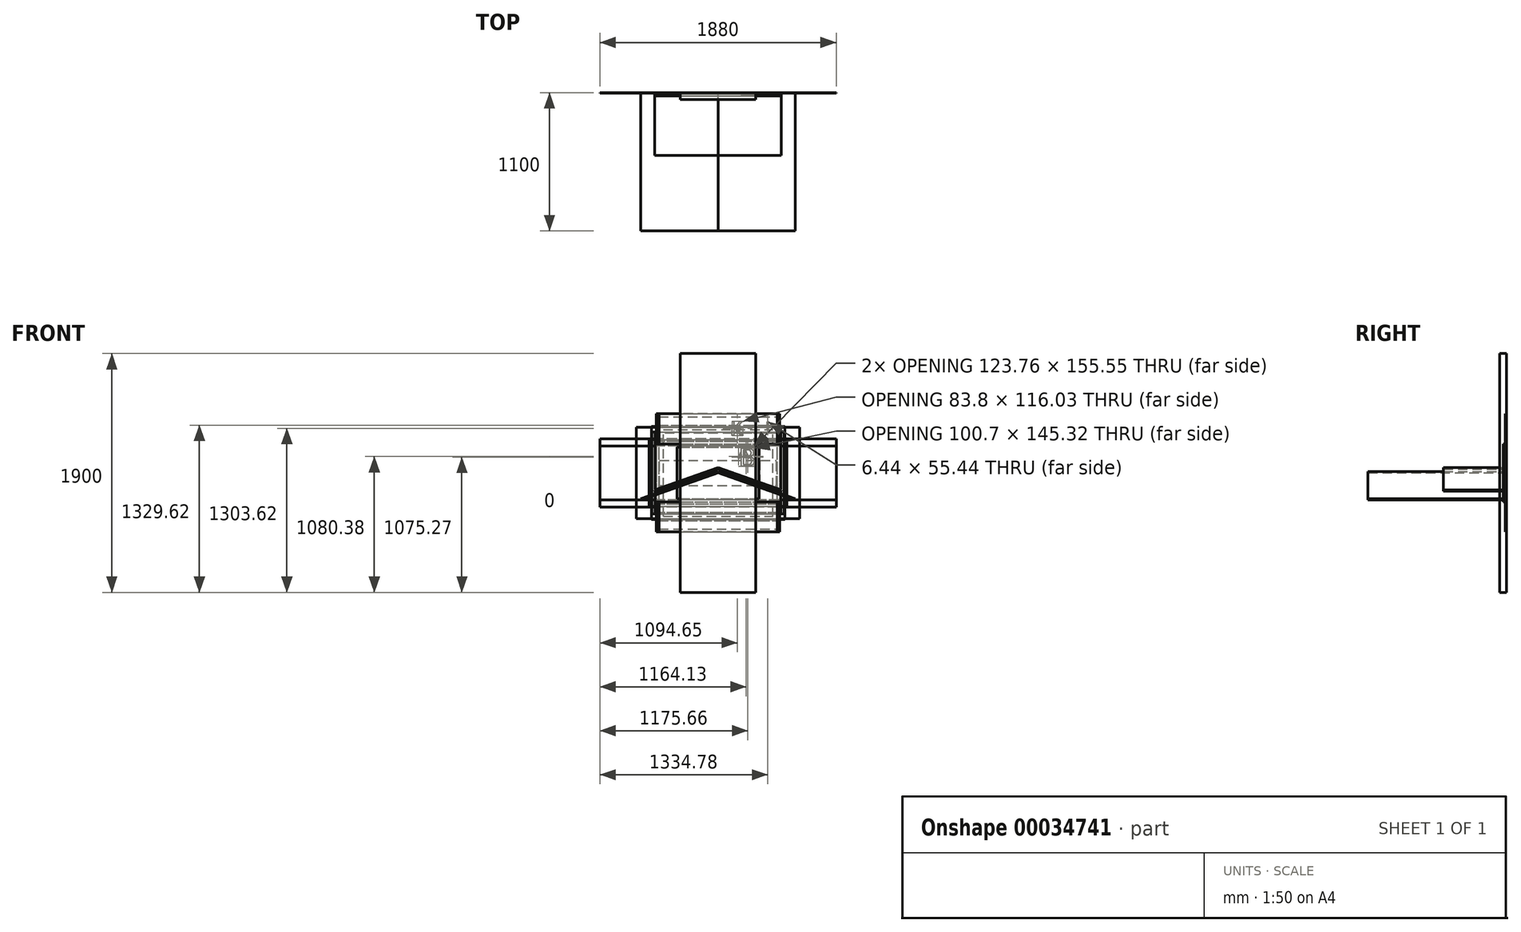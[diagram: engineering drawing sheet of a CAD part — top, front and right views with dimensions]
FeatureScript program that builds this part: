
annotation { "Feature Type Name" : "Feature", "Feature Type Description" : "" }
export const myFeature = defineFeature(function(context is Context, id is Id, definition is map)
    precondition{}
    {
        {
            var Q0;
            Q0=qCreatedBy(makeId("Front.planeOp"),FACE);
            var sketch = newSketch(context, id + "F0", { "sketchPlane" : qUnion([Q0])});
            skLineSegment(sketch, "E0.rect.bottom", {"start": v(500, 315) * mm, "end": v(-500, 315) * mm});
            skLineSegment(sketch, "E0.rect.top", {"start": v(500, -315) * mm, "end": v(-500, -315) * mm});
            skLineSegment(sketch, "E0.rect.left", {"start": v(500, 315) * mm, "end": v(500, -315) * mm});
            skLineSegment(sketch, "E0.rect.right", {"start": v(-500, 315) * mm, "end": v(-500, -315) * mm});
            skPoint(sketch, "E0.rect.middle", {"position": v(0, 0) * mm});
            skSolve(sketch);
        }
        {
            var Q0;
            Q0 = qSketchRegion(id + "F0", true);
            extrude(context, id + "F1", {"entities" : qUnion([Q0]), "depth" : 5 * mm});
        }
        {
            var Q0;
            Q0=makeQuery(id+"F1.opExtrude","CAP_FACE",FACE,{"disambiguationData":[OSD([sQuery(id+"F0.wireOp",EDGE,"E0.rect.bottom"),sQuery(id+"F0.wireOp",EDGE,"E0.rect.top"),sQuery(id+"F0.wireOp",EDGE,"E0.rect.left"),sQuery(id+"F0.wireOp",EDGE,"E0.rect.right")])],"isStart":false});
            var sketch = newSketch(context, id + "F2", { "sketchPlane" : qUnion([Q0])});
            skLineSegment(sketch, "E1.rect.bottom", {"start": v(-470, -470) * mm, "end": v(470, -470) * mm});
            skLineSegment(sketch, "E1.rect.top", {"start": v(-470, 470) * mm, "end": v(470, 470) * mm});
            skLineSegment(sketch, "E1.rect.left", {"start": v(-470, -470) * mm, "end": v(-470, 470) * mm});
            skLineSegment(sketch, "E1.rect.right", {"start": v(470, -470) * mm, "end": v(470, 470) * mm});
            skPoint(sketch, "E1.rect.middle", {"position": v(0, 0) * mm});
            skSolve(sketch);
        }
        {
            var Q0;
            Q0 = qSketchRegion(id + "F2", true);
            extrude(context, id + "F3", {"entities" : qUnion([Q0]), "depth" : 5 * mm});
        }
        {
            var Q0;
            Q0=qCreatedBy(makeId("Front.planeOp"),FACE);
            var sketch = newSketch(context, id + "F4", { "sketchPlane" : qUnion([Q0])});
            skLineSegment(sketch, "E2.rect.bottom", {"start": v(-500, -230) * mm, "end": v(500, -230) * mm});
            skLineSegment(sketch, "E2.rect.top", {"start": v(-500, 230) * mm, "end": v(500, 230) * mm});
            skLineSegment(sketch, "E2.rect.left", {"start": v(-500, -230) * mm, "end": v(-500, 230) * mm});
            skLineSegment(sketch, "E2.rect.right", {"start": v(500, -230) * mm, "end": v(500, 230) * mm});
            skPoint(sketch, "E2.rect.middle", {"position": v(0, 0) * mm});
            skSolve(sketch);
        }
        {
            var Q0;
            Q0 = qSketchRegion(id + "F4", true);
            extrude(context, id + "F5", {"entities" : qUnion([Q0]), "depth" : 25 * mm});
        }
        {
            var Q0;
            Q0=qCreatedBy(makeId("Front.planeOp"),FACE);
            var sketch = newSketch(context, id + "F6", { "sketchPlane" : qUnion([Q0])});
            skLineSegment(sketch, "E3.rect.bottom", {"start": v(500, -250) * mm, "end": v(-500, -250) * mm});
            skLineSegment(sketch, "E3.rect.top", {"start": v(500, 250) * mm, "end": v(-500, 250) * mm});
            skLineSegment(sketch, "E3.rect.left", {"start": v(500, -250) * mm, "end": v(500, 250) * mm});
            skLineSegment(sketch, "E3.rect.right", {"start": v(-500, -250) * mm, "end": v(-500, 250) * mm});
            skPoint(sketch, "E3.rect.middle", {"position": v(0, 0) * mm});
            skSolve(sketch);
        }
        {
            var Q0;
            Q0 = qSketchRegion(id + "F6", true);
            extrude(context, id + "F7", {"entities" : qUnion([Q0]), "depth" : 5 * mm});
        }
        {
            var Q0;
            {var subQ0=makeQuery(id+"F1.opExtrude","CAP_EDGE",EDGE,{"disambiguationData":[OSD([sQuery(id+"F0.wireOp",EDGE,"E0.rect.top")])],"isStart":false});var subQ3=sQuery(id+"F2.wireOp",EDGE,"E1.rect.left");var subQ4=makeQuery(id+"F2.imprint","INTERSECT",VERTEX,{"derivedFrom":[subQ0,subQ3]});Q0=makeQuery(id+"F2.imprint","IMPRINT",FACE,{"disambiguationData":[TD([[makeQuery(id+"F2.imprint","IMPRINT",EDGE,{"disambiguationData":[TD([[subQ4,-1.0]])],"derivedFrom":subQ3}),-1.0]])]});}
            var sketch = newSketch(context, id + "F8", { "sketchPlane" : qUnion([Q0])});
            skText(sketch, "E4", { "text": "A", "fontName": "OpenSans-Regular.ttf"});
            const initialGuessF8  = {"E4": [0.16225, 0.1153, 1, 0, 0.09326]};
            skSetInitialGuess(sketch, initialGuessF8);
            skSolve(sketch);
        }
        {
            var Q0;
            Q0=makeQuery(id+"F8.imprint","IMPRINT",FACE,{"disambiguationData":[TD([[makeQuery(id+"F8.imprint","IMPRINT",EDGE,{"derivedFrom":sQuery(id+"F8.wireOp",EDGE,"E4.sketch_text.stroke-0")}),-1.0]])]});
            extrude(context, id + "F9", {"entities" : qUnion([Q0]), "operationType" : NewBodyOperationType.REMOVE, "oppositeDirection" : true, "depth" : 25 * mm});
        }
        {
            var Q0;
            Q0=makeQuery(id+"F3.opExtrude","CAP_FACE",FACE,{"disambiguationData":[OSD([sQuery(id+"F2.wireOp",EDGE,"E1.rect.bottom"),sQuery(id+"F2.wireOp",EDGE,"E1.rect.top"),sQuery(id+"F2.wireOp",EDGE,"E1.rect.left"),sQuery(id+"F2.wireOp",EDGE,"E1.rect.right")])],"isStart":false});
            var sketch = newSketch(context, id + "F10", { "sketchPlane" : qUnion([Q0])});
            skText(sketch, "E5", { "text": "K", "fontName": "OpenSans-Regular.ttf"});
            const initialGuessF10  = {"E5": [0.0968, 0.2956, 1, 0, 0.11702]};
            skSetInitialGuess(sketch, initialGuessF10);
            skSolve(sketch);
        }
        {
            var Q0;
            Q0 = qSketchRegion(id + "F10", true);
            extrude(context, id + "F11", {"entities" : qUnion([Q0]), "operationType" : NewBodyOperationType.REMOVE, "oppositeDirection" : true, "depth" : 25 * mm});
        }
        {
            var Q0;
            Q0=makeQuery(id+"F5.opExtrude","CAP_FACE",FACE,{"disambiguationData":[OSD([sQuery(id+"F4.wireOp",EDGE,"E2.rect.bottom"),sQuery(id+"F4.wireOp",EDGE,"E2.rect.top"),sQuery(id+"F4.wireOp",EDGE,"E2.rect.left"),sQuery(id+"F4.wireOp",EDGE,"E2.rect.right")])],"isStart":false});
            var sketch = newSketch(context, id + "F12", { "sketchPlane" : qUnion([Q0])});
            skText(sketch, "E6", { "text": "B", "fontName": "OpenSans-Regular.ttf"});
            const initialGuessF12  = {"E6": [0.16534, 0.05261, 1, 0, 0.14656]};
            skSetInitialGuess(sketch, initialGuessF12);
            skSolve(sketch);
        }
        {
            var Q0;
            Q0 = qSketchRegion(id + "F12", true);
            extrude(context, id + "F13", {"entities" : qUnion([Q0]), "operationType" : NewBodyOperationType.REMOVE, "oppositeDirection" : true, "depth" : 25 * mm});
        }
        {
            var Q0;
            Q0=qCreatedBy(makeId("Front.planeOp"),FACE);
            var sketch = newSketch(context, id + "F14", { "sketchPlane" : qUnion([Q0])});
            skLineSegment(sketch, "E7.rect.bottom", {"start": v(-435, -345) * mm, "end": v(435, -345) * mm});
            skLineSegment(sketch, "E7.rect.top", {"start": v(-435, 345) * mm, "end": v(435, 345) * mm});
            skLineSegment(sketch, "E7.rect.left", {"start": v(-435, -345) * mm, "end": v(-435, 345) * mm});
            skLineSegment(sketch, "E7.rect.right", {"start": v(435, -345) * mm, "end": v(435, 345) * mm});
            skPoint(sketch, "E7.rect.middle", {"position": v(0, 0) * mm});
            skSolve(sketch);
        }
        {
            var Q0;
            Q0 = qSketchRegion(id + "F14", true);
            extrude(context, id + "F15", {"entities" : qUnion([Q0]), "depth" : 5 * mm});
        }
        {
            var Q0;
            Q0=qCreatedBy(makeId("Front.planeOp"),FACE);
            var sketch = newSketch(context, id + "F16", { "sketchPlane" : qUnion([Q0])});
            skLineSegment(sketch, "E8.rect.bottom", {"start": v(-490, 380) * mm, "end": v(490, 380) * mm});
            skLineSegment(sketch, "E8.rect.top", {"start": v(-490, -380) * mm, "end": v(490, -380) * mm});
            skLineSegment(sketch, "E8.rect.left", {"start": v(-490, 380) * mm, "end": v(-490, -380) * mm});
            skLineSegment(sketch, "E8.rect.right", {"start": v(490, 380) * mm, "end": v(490, -380) * mm});
            skPoint(sketch, "E8.rect.middle", {"position": v(0, 0) * mm});
            skSolve(sketch);
        }
        {
            var Q0;
            Q0 = qSketchRegion(id + "F16", true);
            extrude(context, id + "F17", {"entities" : qUnion([Q0]), "depth" : 5 * mm});
        }
        {
            var Q0;
            Q0=qCreatedBy(makeId("Front.planeOp"),FACE);
            var sketch = newSketch(context, id + "F18", { "sketchPlane" : qUnion([Q0])});
            skLineSegment(sketch, "E9.rect.bottom", {"start": v(-530, 370) * mm, "end": v(530, 370) * mm});
            skLineSegment(sketch, "E9.rect.top", {"start": v(-530, -370) * mm, "end": v(530, -370) * mm});
            skLineSegment(sketch, "E9.rect.left", {"start": v(-530, 370) * mm, "end": v(-530, -370) * mm});
            skLineSegment(sketch, "E9.rect.right", {"start": v(530, 370) * mm, "end": v(530, -370) * mm});
            skPoint(sketch, "E9.rect.middle", {"position": v(0, 0) * mm});
            skSolve(sketch);
        }
        {
            var Q0;
            Q0 = qSketchRegion(id + "F18", true);
            extrude(context, id + "F19", {"entities" : qUnion([Q0]), "depth" : 5 * mm});
        }
        {
            var Q0;
            Q0=qCreatedBy(makeId("Front.planeOp"),FACE);
            var sketch = newSketch(context, id + "F20", { "sketchPlane" : qUnion([Q0])});
            skLineSegment(sketch, "E10.rect.bottom", {"start": v(-325, 205) * mm, "end": v(325, 205) * mm});
            skLineSegment(sketch, "E10.rect.top", {"start": v(-325, -205) * mm, "end": v(325, -205) * mm});
            skLineSegment(sketch, "E10.rect.left", {"start": v(-325, 205) * mm, "end": v(-325, -205) * mm});
            skLineSegment(sketch, "E10.rect.right", {"start": v(325, 205) * mm, "end": v(325, -205) * mm});
            skPoint(sketch, "E10.rect.middle", {"position": v(0, 0) * mm});
            skSolve(sketch);
        }
        {
            var Q0;
            Q0 = qSketchRegion(id + "F20", true);
            extrude(context, id + "F21", {"entities" : qUnion([Q0]), "depth" : 25 * mm});
        }
        {
            var Q0;
            Q0=qCreatedBy(makeId("Front.planeOp"),FACE);
            var sketch = newSketch(context, id + "F22", { "sketchPlane" : qUnion([Q0])});
            skLineSegment(sketch, "E11.rect.bottom", {"start": v(-525, -325) * mm, "end": v(525, -325) * mm});
            skLineSegment(sketch, "E11.rect.top", {"start": v(-525, 325) * mm, "end": v(525, 325) * mm});
            skLineSegment(sketch, "E11.rect.left", {"start": v(-525, -325) * mm, "end": v(-525, 325) * mm});
            skLineSegment(sketch, "E11.rect.right", {"start": v(525, -325) * mm, "end": v(525, 325) * mm});
            skPoint(sketch, "E11.rect.middle", {"position": v(0, 0) * mm});
            skSolve(sketch);
        }
        {
            var Q0;
            Q0 = qSketchRegion(id + "F22", true);
            extrude(context, id + "F23", {"entities" : qUnion([Q0]), "depth" : 5 * mm});
        }
        {
            var Q0;
            Q0=qCreatedBy(makeId("Front.planeOp"),FACE);
            var sketch = newSketch(context, id + "F24", { "sketchPlane" : qUnion([Q0])});
            skLineSegment(sketch, "E12.rect.bottom", {"start": v(490, 470) * mm, "end": v(-490, 470) * mm});
            skLineSegment(sketch, "E12.rect.top", {"start": v(490, -470) * mm, "end": v(-490, -470) * mm});
            skLineSegment(sketch, "E12.rect.left", {"start": v(490, 470) * mm, "end": v(490, -470) * mm});
            skLineSegment(sketch, "E12.rect.right", {"start": v(-490, 470) * mm, "end": v(-490, -470) * mm});
            skPoint(sketch, "E12.rect.middle", {"position": v(0, 0) * mm});
            skSolve(sketch);
        }
        {
            var Q0;
            Q0 = qSketchRegion(id + "F24", true);
            extrude(context, id + "F25", {"entities" : qUnion([Q0]), "depth" : 5 * mm});
        }
        {
            var Q0;
            Q0=makeQuery(id+"F25.opExtrude","CAP_FACE",FACE,{"disambiguationData":[OSD([sQuery(id+"F24.wireOp",EDGE,"E12.rect.bottom"),sQuery(id+"F24.wireOp",EDGE,"E12.rect.top"),sQuery(id+"F24.wireOp",EDGE,"E12.rect.left"),sQuery(id+"F24.wireOp",EDGE,"E12.rect.right")])],"isStart":false});
            var sketch = newSketch(context, id + "F26", { "sketchPlane" : qUnion([Q0])});
            skText(sketch, "E13", { "text": "I", "fontName": "OpenSans-Regular.ttf"});
            const initialGuessF26  = {"E13": [0.38394, 0.3519, 1, 0, 0.05591]};
            skSetInitialGuess(sketch, initialGuessF26);
            skSolve(sketch);
        }
        {
            var Q0;
            Q0 = qSketchRegion(id + "F26", true);
            extrude(context, id + "F27", {"entities" : qUnion([Q0]), "operationType" : NewBodyOperationType.REMOVE, "oppositeDirection" : true, "depth" : 25 * mm});
        }
        {
            var Q0;
            Q0=qCreatedBy(makeId("Front.planeOp"),FACE);
            var sketch = newSketch(context, id + "F28", { "sketchPlane" : qUnion([Q0])});
            skLineSegment(sketch, "E14.rect.bottom", {"start": v(-470, -445) * mm, "end": v(470, -445) * mm});
            skLineSegment(sketch, "E14.rect.top", {"start": v(-470, 445) * mm, "end": v(470, 445) * mm});
            skLineSegment(sketch, "E14.rect.left", {"start": v(-470, -445) * mm, "end": v(-470, 445) * mm});
            skLineSegment(sketch, "E14.rect.right", {"start": v(470, -445) * mm, "end": v(470, 445) * mm});
            skPoint(sketch, "E14.rect.middle", {"position": v(0, 0) * mm});
            skSolve(sketch);
        }
        {
            var Q0;
            Q0 = qSketchRegion(id + "F28", true);
            extrude(context, id + "F29", {"entities" : qUnion([Q0]), "depth" : 5 * mm});
        }
        {
            var Q0;
            Q0=qCreatedBy(makeId("Front.planeOp"),FACE);
            var sketch = newSketch(context, id + "F30", { "sketchPlane" : qUnion([Q0])});
            skLineSegment(sketch, "E15.rect.bottom", {"start": v(-650, -365) * mm, "end": v(650, -365) * mm});
            skLineSegment(sketch, "E15.rect.top", {"start": v(-650, 365) * mm, "end": v(650, 365) * mm});
            skLineSegment(sketch, "E15.rect.left", {"start": v(-650, -365) * mm, "end": v(-650, 365) * mm});
            skLineSegment(sketch, "E15.rect.right", {"start": v(650, -365) * mm, "end": v(650, 365) * mm});
            skPoint(sketch, "E15.rect.middle", {"position": v(0, 0) * mm});
            skSolve(sketch);
        }
        {
            var Q0;
            Q0 = qSketchRegion(id + "F30", true);
            extrude(context, id + "F31", {"entities" : qUnion([Q0]), "depth" : 5 * mm});
        }
        {
            var Q0;
            Q0=qCreatedBy(makeId("Front.planeOp"),FACE);
            var sketch = newSketch(context, id + "F32", { "sketchPlane" : qUnion([Q0])});
            skLineSegment(sketch, "E16.rect.bottom", {"start": v(-547.5, 265) * mm, "end": v(547.5, 265) * mm});
            skLineSegment(sketch, "E16.rect.top", {"start": v(-547.5, -265) * mm, "end": v(547.5, -265) * mm});
            skLineSegment(sketch, "E16.rect.left", {"start": v(-547.5, 265) * mm, "end": v(-547.5, -265) * mm});
            skLineSegment(sketch, "E16.rect.right", {"start": v(547.5, 265) * mm, "end": v(547.5, -265) * mm});
            skPoint(sketch, "E16.rect.middle", {"position": v(0, 0) * mm});
            skSolve(sketch);
        }
        {
            var Q0;
            Q0 = qSketchRegion(id + "F32", true);
            extrude(context, id + "F33", {"entities" : qUnion([Q0]), "depth" : 5 * mm});
        }
        {
            var Q0;
            Q0=qCreatedBy(makeId("Front.planeOp"),FACE);
            var sketch = newSketch(context, id + "F34", { "sketchPlane" : qUnion([Q0])});
            skLineSegment(sketch, "E17", {"start": v(-610.17, -213.68) * mm, "end": v(0, 0) * mm});
            skLineSegment(sketch, "E18", {"start": v(0, 0) * mm, "end": v(610.17, -213.68) * mm});
            skLineSegment(sketch, "E19", {"start": v(-610.17, -213.68) * mm, "end": v(610.17, -213.68) * mm, "construction": true});
            skLineSegment(sketch, "E20", {"start": v(-610.17, -213.68) * mm, "end": v(-613.47, -204.24) * mm});
            skLineSegment(sketch, "E21", {"start": v(-613.47, -204.24) * mm, "end": v(0, 10.6) * mm});
            skLineSegment(sketch, "E22", {"start": v(0, 10.6) * mm, "end": v(613.47, -204.24) * mm});
            skLineSegment(sketch, "E23", {"start": v(613.47, -204.24) * mm, "end": v(610.17, -213.68) * mm});
            skSolve(sketch);
        }
        {
            var Q0;
            Q0 = qSketchRegion(id + "F34", true);
            extrude(context, id + "F35", {"entities" : qUnion([Q0]), "depth" : 1100 * mm});
        }
        {
            var Q0;
            Q0=qCreatedBy(makeId("Front.planeOp"),FACE);
            var sketch = newSketch(context, id + "F36", { "sketchPlane" : qUnion([Q0])});
            skLineSegment(sketch, "E24.rect.bottom", {"start": v(940, 270) * mm, "end": v(-940, 270) * mm});
            skLineSegment(sketch, "E24.rect.top", {"start": v(940, -270) * mm, "end": v(-940, -270) * mm});
            skLineSegment(sketch, "E24.rect.left", {"start": v(940, 270) * mm, "end": v(940, -270) * mm});
            skLineSegment(sketch, "E24.rect.right", {"start": v(-940, 270) * mm, "end": v(-940, -270) * mm});
            skPoint(sketch, "E24.rect.middle", {"position": v(0, 0) * mm});
            skSolve(sketch);
        }
        {
            var Q0;
            Q0 = qSketchRegion(id + "F36", true);
            extrude(context, id + "F37", {"entities" : qUnion([Q0]), "depth" : 5 * mm});
        }
        {
            var Q0;
            Q0=qCreatedBy(makeId("Front.planeOp"),FACE);
            var sketch = newSketch(context, id + "F38", { "sketchPlane" : qUnion([Q0])});
            skLineSegment(sketch, "E25.rect.bottom", {"start": v(940, 215) * mm, "end": v(-940, 215) * mm});
            skLineSegment(sketch, "E25.rect.top", {"start": v(940, -215) * mm, "end": v(-940, -215) * mm});
            skLineSegment(sketch, "E25.rect.left", {"start": v(940, 215) * mm, "end": v(940, -215) * mm});
            skLineSegment(sketch, "E25.rect.right", {"start": v(-940, 215) * mm, "end": v(-940, -215) * mm});
            skPoint(sketch, "E25.rect.middle", {"position": v(0, 0) * mm});
            skSolve(sketch);
        }
        {
            var Q0;
            Q0 = qSketchRegion(id + "F38", true);
            extrude(context, id + "F39", {"entities" : qUnion([Q0]), "depth" : 5 * mm});
        }
        {
            var Q0;
            Q0=qCreatedBy(makeId("Front.planeOp"),FACE);
            var sketch = newSketch(context, id + "F40", { "sketchPlane" : qUnion([Q0])});
            skLineSegment(sketch, "E26.rect.bottom", {"start": v(-465, -100) * mm, "end": v(465, -100) * mm});
            skLineSegment(sketch, "E26.rect.top", {"start": v(-465, 100) * mm, "end": v(465, 100) * mm});
            skLineSegment(sketch, "E26.rect.left", {"start": v(-465, -100) * mm, "end": v(-465, 100) * mm});
            skLineSegment(sketch, "E26.rect.right", {"start": v(465, -100) * mm, "end": v(465, 100) * mm});
            skPoint(sketch, "E26.rect.middle", {"position": v(0, 0) * mm});
            skSolve(sketch);
        }
        {
            var Q0;
            Q0 = qSketchRegion(id + "F40", true);
            extrude(context, id + "F41", {"entities" : qUnion([Q0]), "depth" : 5 * mm});
        }
        {
            var Q0;
            Q0=qCreatedBy(makeId("Front.planeOp"),FACE);
            var sketch = newSketch(context, id + "F42", { "sketchPlane" : qUnion([Q0])});
            skLineSegment(sketch, "E27.rect.bottom", {"start": v(330, 215) * mm, "end": v(-330, 215) * mm});
            skLineSegment(sketch, "E27.rect.top", {"start": v(330, -215) * mm, "end": v(-330, -215) * mm});
            skLineSegment(sketch, "E27.rect.left", {"start": v(330, 215) * mm, "end": v(330, -215) * mm});
            skLineSegment(sketch, "E27.rect.right", {"start": v(-330, 215) * mm, "end": v(-330, -215) * mm});
            skPoint(sketch, "E27.rect.middle", {"position": v(0, 0) * mm});
            skSolve(sketch);
        }
        {
            var Q0;
            Q0 = qSketchRegion(id + "F42", true);
            extrude(context, id + "F43", {"entities" : qUnion([Q0]), "depth" : 5 * mm});
        }
        {
            var Q0;
            Q0=qCreatedBy(makeId("Front.planeOp"),FACE);
            var sketch = newSketch(context, id + "F44", { "sketchPlane" : qUnion([Q0])});
            skLineSegment(sketch, "E28", {"start": v(-500.21, -143.66) * mm, "end": v(0, 31.52) * mm});
            skLineSegment(sketch, "E29", {"start": v(1.03, 42.47) * mm, "end": v(-503.52, -134.22) * mm});
            skLineSegment(sketch, "E30", {"start": v(-503.52, -134.22) * mm, "end": v(-500.21, -143.66) * mm});
            skLineSegment(sketch, "E31", {"start": v(0, 165.94) * mm, "end": v(0, 0) * mm, "construction": true});
            skLineSegment(sketch, "E32.MirrorCS", {"start": v(503.52, -134.22) * mm, "end": v(500.21, -143.66) * mm});
            skLineSegment(sketch, "E33.MirrorCS", {"start": v(500.21, -143.66) * mm, "end": v(0, 31.52) * mm});
            skLineSegment(sketch, "E34.MirrorCS", {"start": v(-1.03, 42.47) * mm, "end": v(503.52, -134.22) * mm});
            skSolve(sketch);
        }
        {
            var Q0;
            Q0 = qSketchRegion(id + "F44", true);
            extrude(context, id + "F45", {"entities" : qUnion([Q0]), "depth" : 500 * mm});
        }
        {
            var Q0;
            Q0=qCreatedBy(makeId("Front.planeOp"),FACE);
            var sketch = newSketch(context, id + "F46", { "sketchPlane" : qUnion([Q0])});
            skLineSegment(sketch, "E35.rect.bottom", {"start": v(-300, 950) * mm, "end": v(300, 950) * mm});
            skLineSegment(sketch, "E35.rect.top", {"start": v(-300, -950) * mm, "end": v(300, -950) * mm});
            skLineSegment(sketch, "E35.rect.left", {"start": v(-300, 950) * mm, "end": v(-300, -950) * mm});
            skLineSegment(sketch, "E35.rect.right", {"start": v(300, 950) * mm, "end": v(300, -950) * mm});
            skPoint(sketch, "E35.rect.middle", {"position": v(0, 0) * mm});
            skSolve(sketch);
        }
        {
            var Q0;
            Q0 = qSketchRegion(id + "F46", true);
            extrude(context, id + "F47", {"entities" : qUnion([Q0]), "depth" : 55 * mm});
        }
    });
